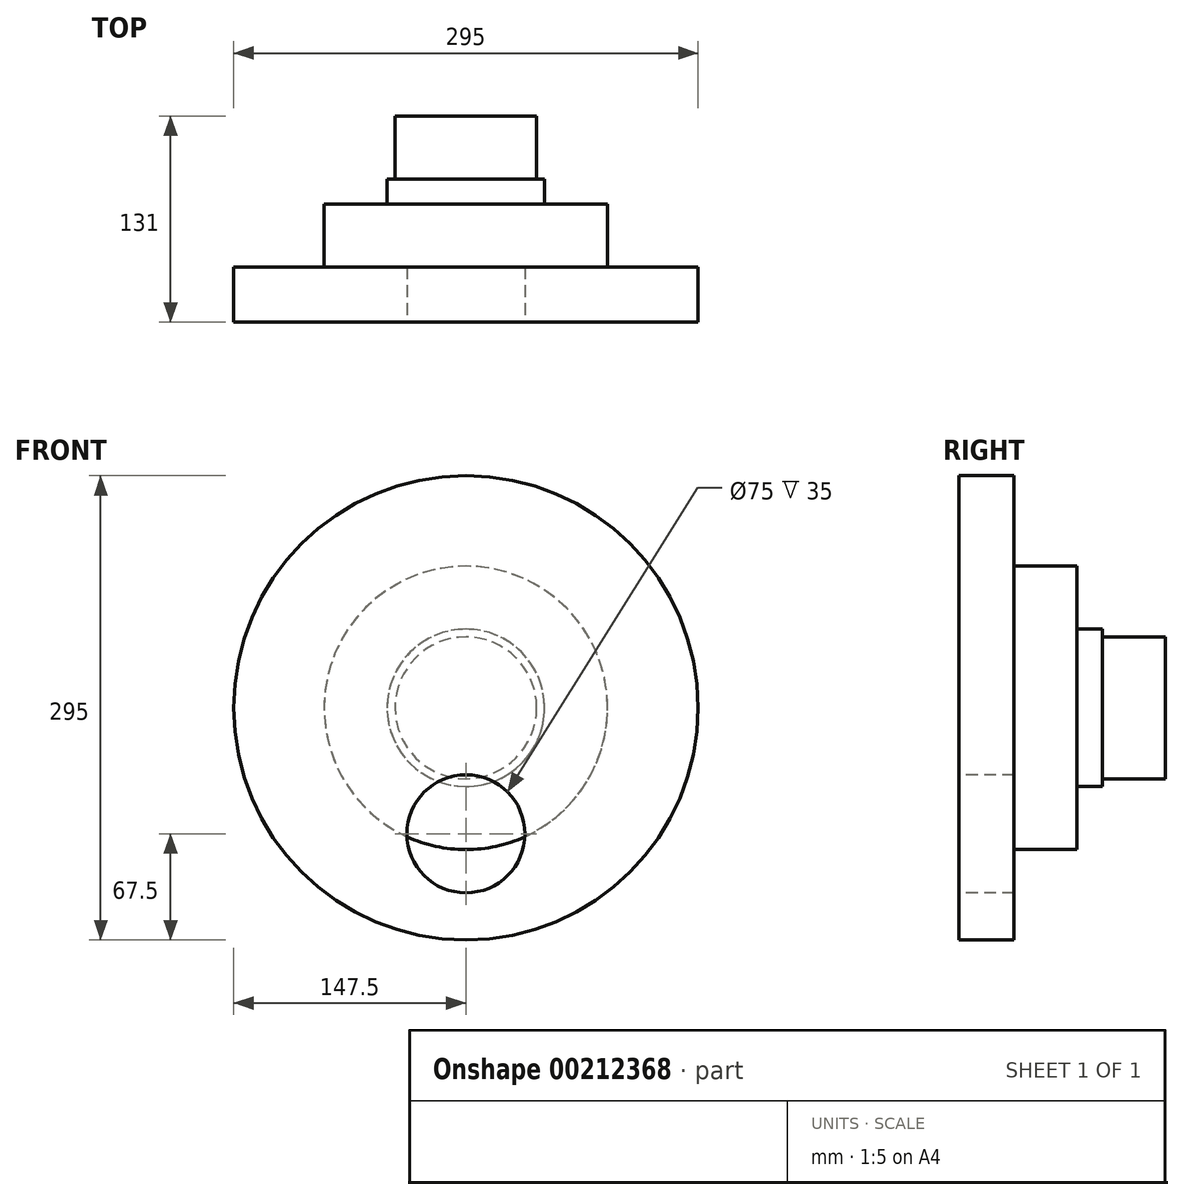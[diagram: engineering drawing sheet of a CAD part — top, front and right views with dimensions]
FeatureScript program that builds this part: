
annotation { "Feature Type Name" : "Feature", "Feature Type Description" : "" }
export const myFeature = defineFeature(function(context is Context, id is Id, definition is map)
    precondition{}
    {
        {
            var Q0;
            Q0=qCreatedBy(makeId("Front.planeOp"),FACE);
            var sketch = newSketch(context, id + "F0", { "sketchPlane" : qUnion([Q0])});
            skCircle(sketch, "E0", {"center": v(0, 0) * mm, "radius": 147.5 * mm});
            skSolve(sketch);
        }
        {
            var Q0;
            Q0=makeQuery(id+"F0.imprint","IMPRINT",FACE,{"disambiguationData":[TD([[makeQuery(id+"F0.imprint","IMPRINT",EDGE,{"derivedFrom":sQuery(id+"F0.wireOp",EDGE,"E0")}),1.0]])]});
            extrude(context, id + "F1", {"entities" : qUnion([Q0]), "depth" : 35 * mm});
        }
        {
            var Q0;
            Q0=makeQuery(id+"F1.opExtrude","CAP_FACE",FACE,{"disambiguationData":[OSD([sQuery(id+"F0.wireOp",EDGE,"E0")])],"isStart":true});
            var sketch = newSketch(context, id + "F2", { "sketchPlane" : qUnion([Q0])});
            skCircle(sketch, "E1", {"center": v(0, 0) * mm, "radius": 50 * mm});
            skSolve(sketch);
        }
        {
            var Q0;
            Q0=makeQuery(id+"F2.imprint","IMPRINT",FACE,{"disambiguationData":[TD([[makeQuery(id+"F2.imprint","IMPRINT",EDGE,{"derivedFrom":sQuery(id+"F2.wireOp",EDGE,"E1")}),1.0]])]});
            extrude(context, id + "F3", {"entities" : qUnion([Q0]), "operationType" : NewBodyOperationType.ADD, "depth" : 56 * mm});
        }
        {
            var Q0;
            Q0=makeQuery(id+"F3.opExtrude","CAP_FACE",FACE,{"disambiguationData":[OSD([sQuery(id+"F2.wireOp",EDGE,"E1")])],"isStart":false});
            var sketch = newSketch(context, id + "F4", { "sketchPlane" : qUnion([Q0])});
            skCircle(sketch, "E2", {"center": v(0, 0) * mm, "radius": 45 * mm});
            skSolve(sketch);
        }
        {
            var Q0;
            Q0=makeQuery(id+"F4.imprint","IMPRINT",FACE,{"disambiguationData":[TD([[makeQuery(id+"F4.imprint","IMPRINT",EDGE,{"derivedFrom":sQuery(id+"F4.wireOp",EDGE,"E2")}),1.0]])]});
            extrude(context, id + "F5", {"entities" : qUnion([Q0]), "operationType" : NewBodyOperationType.ADD, "depth" : 40 * mm});
        }
        {
            var Q0;
            Q0=makeQuery(id+"F1.opExtrude","CAP_FACE",FACE,{"disambiguationData":[OSD([sQuery(id+"F0.wireOp",EDGE,"E0")])],"isStart":false});
            var sketch = newSketch(context, id + "F6", { "sketchPlane" : qUnion([Q0])});
            skCircle(sketch, "E3", {"center": v(0, 0) * mm, "radius": 80 * mm});
            skCircle(sketch, "E4", {"center": v(0, -80) * mm, "radius": 37.5 * mm});
            skSolve(sketch);
        }
        {
            var Q0;
            {var subQ0=sQuery(id+"F6.wireOp",EDGE,"E4");var subQ1=sQuery(id+"F6.wireOp",EDGE,"E3");var subQ2=makeQuery(id+"F6.imprint","INTERSECT",VERTEX,{"disambiguationData":[OD(0.0)],"derivedFrom":[subQ1,subQ0]});Q0=makeQuery(id+"F6.imprint","IMPRINT",FACE,{"disambiguationData":[TD([[makeQuery(id+"F6.imprint","IMPRINT",EDGE,{"disambiguationData":[TD([[subQ2,-1.0]])],"derivedFrom":subQ1}),-1.0]])]});}
            var Q1;
            {var subQ0=sQuery(id+"F6.wireOp",EDGE,"E4");var subQ1=sQuery(id+"F6.wireOp",EDGE,"E3");var subQ2=makeQuery(id+"F6.imprint","INTERSECT",VERTEX,{"disambiguationData":[OD(0.0)],"derivedFrom":[subQ1,subQ0]});Q1=makeQuery(id+"F6.imprint","IMPRINT",FACE,{"disambiguationData":[TD([[makeQuery(id+"F6.imprint","IMPRINT",EDGE,{"disambiguationData":[TD([[subQ2,-1.0]])],"derivedFrom":subQ1}),1.0]])]});}
            extrude(context, id + "F7", {"entities" : qUnion([Q0, Q1]), "operationType" : NewBodyOperationType.REMOVE, "oppositeDirection" : true, "depth" : 40 * mm});
        }
        {
            var Q0;
            Q0=qCreatedBy(makeId("Front.planeOp"),FACE);
            var sketch = newSketch(context, id + "F8", { "sketchPlane" : qUnion([Q0])});
            skCircle(sketch, "E5", {"center": v(0, 0) * mm, "radius": 90 * mm});
            skSolve(sketch);
        }
        {
            var Q0;
            Q0=makeQuery(id+"F8.imprint","IMPRINT",FACE,{"disambiguationData":[TD([[makeQuery(id+"F8.imprint","IMPRINT",EDGE,{"derivedFrom":sQuery(id+"F8.wireOp",EDGE,"E5")}),1.0]])]});
            extrude(context, id + "F9", {"entities" : qUnion([Q0]), "operationType" : NewBodyOperationType.ADD, "oppositeDirection" : true, "depth" : 40 * mm});
        }
    });
